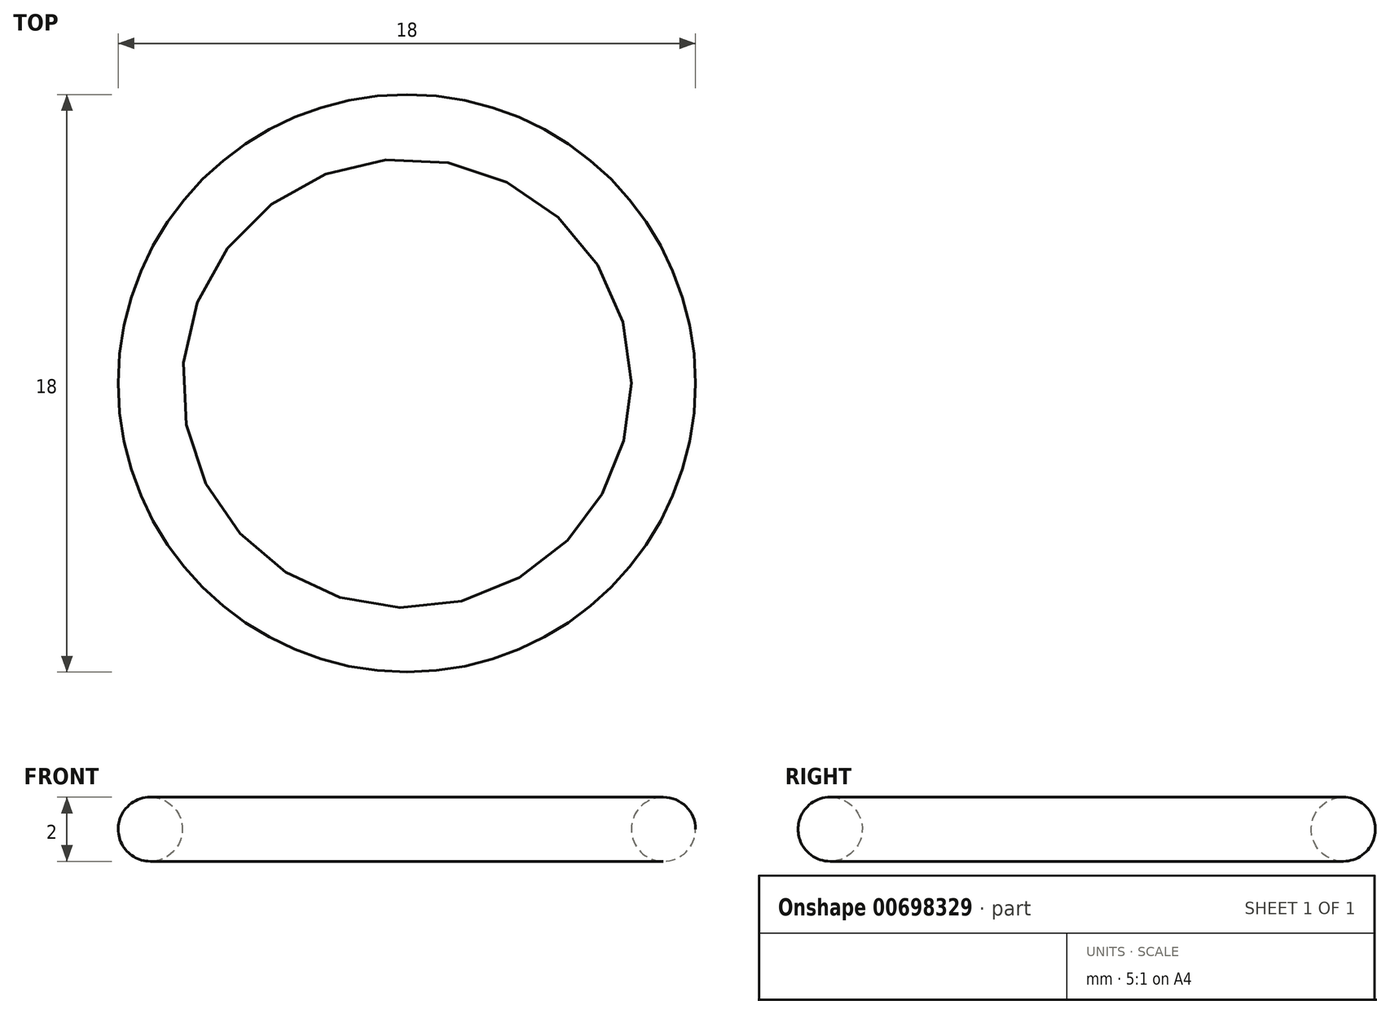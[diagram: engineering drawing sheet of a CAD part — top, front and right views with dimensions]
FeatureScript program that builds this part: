
annotation { "Feature Type Name" : "Feature", "Feature Type Description" : "" }
export const myFeature = defineFeature(function(context is Context, id is Id, definition is map)
    precondition{}
    {
        {
            var Q0;
            Q0=qCreatedBy(makeId("Top.planeOp"),FACE);
            var sketch = newSketch(context, id + "F0", { "sketchPlane" : qUnion([Q0])});
            skCircle(sketch, "E0", {"center": v(0, 0) * mm, "radius": 8 * mm});
            skSolve(sketch);
        }
        {
            var Q0;
            Q0=qCreatedBy(makeId("Right.planeOp"),FACE);
            var sketch = newSketch(context, id + "F1", { "sketchPlane" : qUnion([Q0])});
            skLineSegment(sketch, "E1.0", {"start": v(-8, 0) * mm, "end": v(8, 0) * mm, "construction": true});
            skCircle(sketch, "E2", {"center": v(-8, 0) * mm, "radius": 1 * mm});
            skSolve(sketch);
        }
        {
            var Q0;
            Q0=makeQuery(id+"F1.imprint","IMPRINT",FACE,{"disambiguationData":[TD([[makeQuery(id+"F1.imprint","IMPRINT",EDGE,{"derivedFrom":sQuery(id+"F1.wireOp",EDGE,"E2")}),1.0]])]});
            var Q1;
            Q1=sQuery(id+"F0.wireOp",EDGE,"E0");
            sweep(context, id + "F2", {"profiles" : qUnion([Q0]), "path" : qUnion([Q1])});
        }
    });
